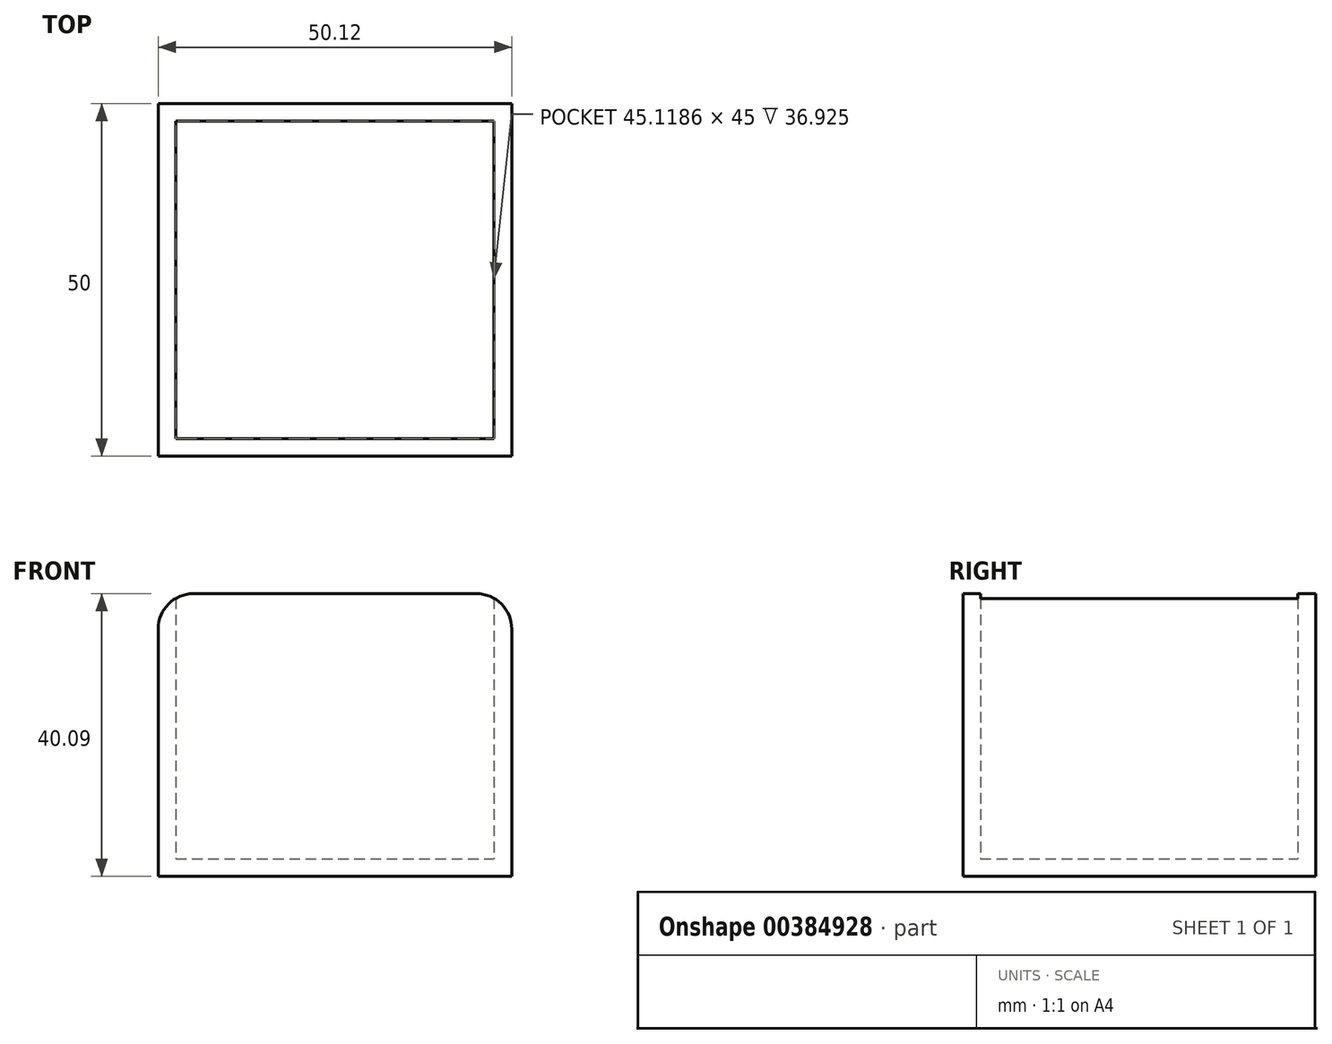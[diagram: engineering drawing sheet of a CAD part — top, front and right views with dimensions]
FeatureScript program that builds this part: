
annotation { "Feature Type Name" : "Feature", "Feature Type Description" : "" }
export const myFeature = defineFeature(function(context is Context, id is Id, definition is map)
    precondition{}
    {
        {
            var Q0;
            Q0=qCreatedBy(makeId("Front.planeOp"),FACE);
            var sketch = newSketch(context, id + "F0", { "sketchPlane" : qUnion([Q0])});
            skLineSegment(sketch, "E0.bottom", {"start": v(-25.26, 27) * mm, "end": v(24.86, 27) * mm});
            skLineSegment(sketch, "E0.top", {"start": v(-25.26, -13.1) * mm, "end": v(24.86, -13.1) * mm});
            skLineSegment(sketch, "E0.left", {"start": v(-25.26, 27) * mm, "end": v(-25.26, -13.1) * mm});
            skLineSegment(sketch, "E0.right", {"start": v(24.86, 27) * mm, "end": v(24.86, -13.1) * mm});
            skSolve(sketch);
        }
        {
            var Q0;
            Q0=makeQuery(id+"F0.imprint","IMPRINT",FACE,{"disambiguationData":[TD([[makeQuery(id+"F0.imprint","IMPRINT",EDGE,{"derivedFrom":sQuery(id+"F0.wireOp",EDGE,"E0.bottom")}),-1.0]])]});
            var Q1;
            Q1 = qSketchRegion(id + "F0", true);
            extrude(context, id + "F1", {"entities" : qUnion([Q0, Q1]), "depth" : 50 * mm});
        }
        {
            var Q0;
            Q0=makeQuery(id+"F1.opExtrude","SWEPT_FACE",FACE,{"disambiguationData":[OSD([sQuery(id+"F0.wireOp",EDGE,"E0.bottom")])]});
            shell(context, id + "F2", {"entities" : qUnion([Q0]), "thickness" : 2.5 * mm});
        }
        {
            var Q0;
            Q0=makeQuery(id+"F1.opExtrude","SWEPT_EDGE",EDGE,{"disambiguationData":[OSD([sQuery(id+"F0.wireOp",EDGE,"E0.bottom"),sQuery(id+"F0.wireOp",EDGE,"E0.right")])]});
            fillet(context, id + "F3", {"entities" : qUnion([Q0]), "radius" : 5 * mm, "tangentPropagation" : true, "allowEdgeOverflow" : false});
        }
        {
            var Q0;
            Q0=makeQuery(id+"F1.opExtrude","SWEPT_EDGE",EDGE,{"disambiguationData":[OSD([sQuery(id+"F0.wireOp",EDGE,"E0.bottom"),sQuery(id+"F0.wireOp",EDGE,"E0.left")])]});
            fillet(context, id + "F4", {"entities" : qUnion([Q0]), "radius" : 5 * mm, "tangentPropagation" : true, "allowEdgeOverflow" : false});
        }
    });
